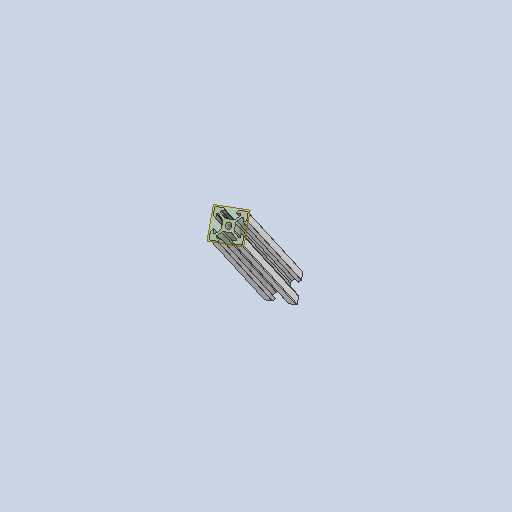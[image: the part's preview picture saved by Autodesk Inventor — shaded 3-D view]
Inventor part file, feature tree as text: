
AUTODESK INVENTOR PART (.ipt)
format: ipt  version: 2024.2 (Build 282272000, 272)  size: 253,440 bytes
history: native  units: mm
features: other x5, extrude x1, sketch x1, reference x1
ambient origin geometry x8: Origin, YZ Plane, XZ Plane, XY Plane, X Axis, Y Axis, Z Axis, Center Point
bodies: Body1 (feature_tree)
feature tree (8):
  other  "Твердое тело1"
  other  "РабПлоскость1"
  extrude  "Выдавливание1"  Depth=250.0mm TaperAngle=0.0deg
  sketch  "Эскиз1"
  reference  "Ссылка1"
  other  "<userpath>\Documents\Artist-v2\3D\Робот.iam"
  other  "Робот.iam"
  other  "2020 V-Slot Profile Extrusion:1"
